# Revit family: Haworth_Janus_SEE_CenterModule_Closed
name_source: partatom
category: Furniture
revit_build: Autodesk Revit 2018 (Build: 20170223_1515(x64)
units: mm (PartAtom-declared; Revit-internal decimal feet)

## family parameters
Always vertical = Yes
Cut with Voids When Loaded = No
OmniClass Number = 23.40.20.00
OmniClass Title = General Furniture and Specialties
Room Calculation Point = No
Shared = No
Work Plane-Based = No

## types (3) — shared parameters
Actual Depth = 36 1/4"
Actual Height = 31"
Assembly Code = E2020200
Cushion = Yes
Frame = Yes
Glide Finish = Haworth _ Polymer _ Black
Manufacturer = Haworth
Revision = 2
Size = Verify Final Dim. w/ Haworth
URL = http://www.haworth.com
URL - Product = https://www.haworth.com
Warranty = https://www.haworth.com
With Seat Cushion = Yes

## per-type parameters (varying)
| type | Actual Width | Description | Large | Medium | Wide |
| HCJC-SE-MESC-J | 26" | Haworth - Janus - SEE! - Center Module Closed - Medium | No | Yes | No |
| HCJC-SE-MEWC-J | 36 1/4" | Haworth - Janus - SEE! - Center Module Closed - Wide | No | No | Yes |
| HCJC-SE-MEXC-J | 54 1/4" | Haworth - Janus - SEE! - Center Module Closed - Large | Yes | No | No |

note: column(s) folded — value = type name in every type: Model

## geometry (parser evidence)
native form markers: Sweep x4
no freeform markers — native parametric forms only
